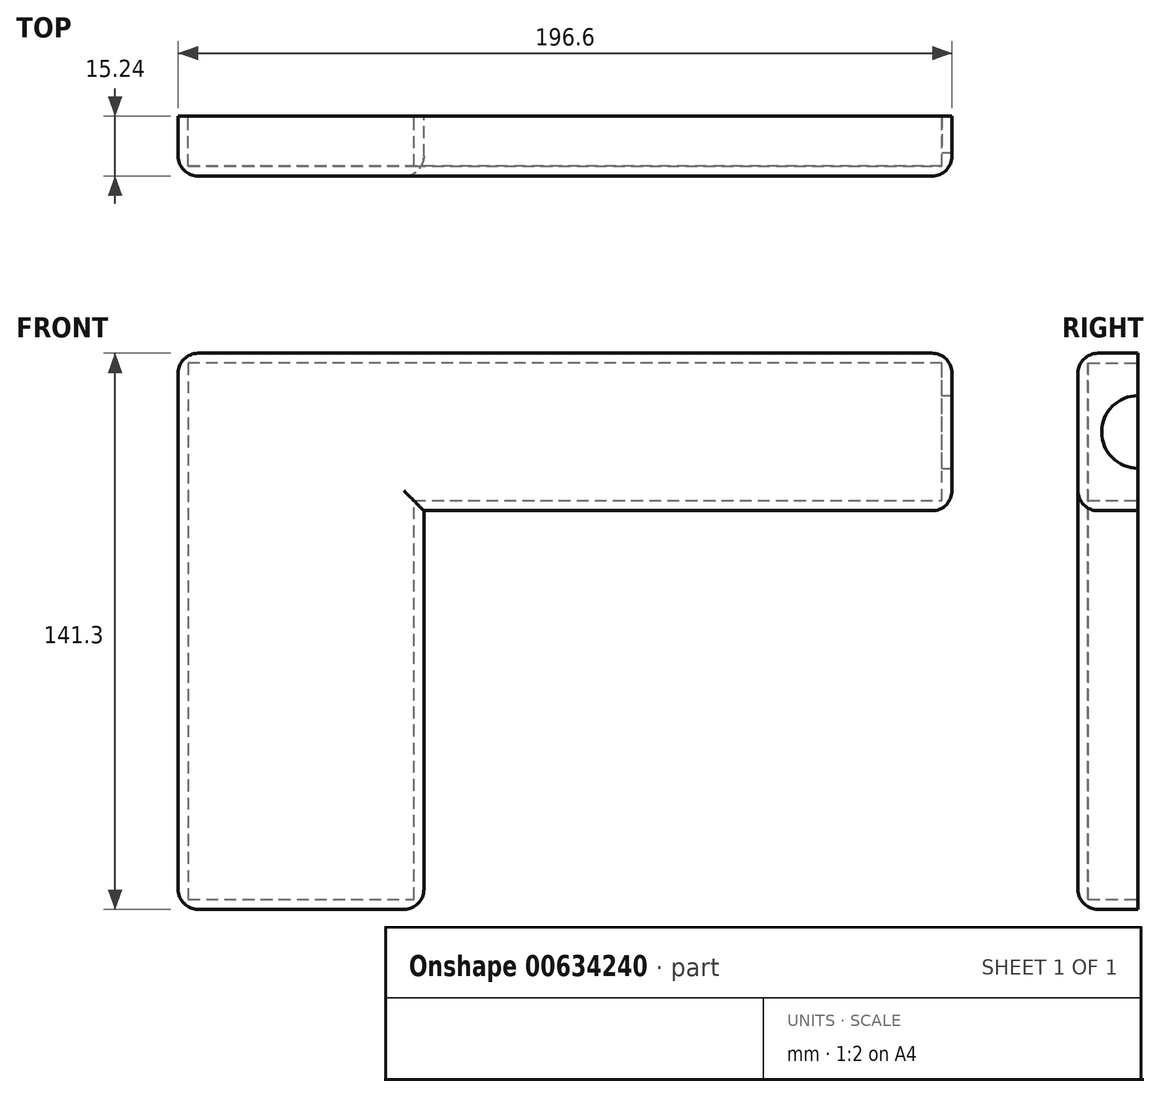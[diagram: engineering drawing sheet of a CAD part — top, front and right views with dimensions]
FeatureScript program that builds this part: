
annotation { "Feature Type Name" : "Feature", "Feature Type Description" : "" }
export const myFeature = defineFeature(function(context is Context, id is Id, definition is map)
    precondition{}
    {
        {
            var Q0;
            Q0=qCreatedBy(makeId("Front.planeOp"),FACE);
            var sketch = newSketch(context, id + "F0", { "sketchPlane" : qUnion([Q0])});
            skLineSegment(sketch, "E0", {"start": v(86.57, 57.04) * mm, "end": v(-110.03, 57.04) * mm});
            skLineSegment(sketch, "E1", {"start": v(-110.03, 57.04) * mm, "end": v(-110.03, -84.26) * mm});
            skLineSegment(sketch, "E2", {"start": v(-110.03, -84.26) * mm, "end": v(-47.62, -84.26) * mm});
            skLineSegment(sketch, "E3", {"start": v(-47.62, -84.26) * mm, "end": v(-47.62, 17.04) * mm});
            skLineSegment(sketch, "E4", {"start": v(-47.62, 17.04) * mm, "end": v(86.57, 17.04) * mm});
            skLineSegment(sketch, "E5", {"start": v(86.57, 17.04) * mm, "end": v(86.57, 57.04) * mm});
            skSolve(sketch);
        }
        {
            var Q0;
            Q0=makeQuery(id+"F0.imprint","IMPRINT",FACE,{"disambiguationData":[TD([[makeQuery(id+"F0.imprint","IMPRINT",EDGE,{"derivedFrom":sQuery(id+"F0.wireOp",EDGE,"E0")}),1.0]])]});
            extrude(context, id + "F1", {"entities" : qUnion([Q0]), "depth" : 15.24 * mm, "offsetDistance" : 25.4 * mm});
        }
        {
            var Q0;
            Q0=makeQuery(id+"F1.opExtrude","CAP_FACE",FACE,{"disambiguationData":[OSD([sQuery(id+"F0.wireOp",EDGE,"E0"),sQuery(id+"F0.wireOp",EDGE,"E1"),sQuery(id+"F0.wireOp",EDGE,"E2"),sQuery(id+"F0.wireOp",EDGE,"E3"),sQuery(id+"F0.wireOp",EDGE,"E4"),sQuery(id+"F0.wireOp",EDGE,"E5")])],"isStart":true});
            shell(context, id + "F2", {"entities" : qUnion([Q0]), "thickness" : 2.54 * mm});
        }
        {
            var Q0;
            Q0=makeQuery(id+"F1.opExtrude","CAP_EDGE",EDGE,{"disambiguationData":[OSD([sQuery(id+"F0.wireOp",EDGE,"E1")])],"isStart":false});
            var Q1;
            Q1=makeQuery(id+"F1.opExtrude","CAP_EDGE",EDGE,{"disambiguationData":[OSD([sQuery(id+"F0.wireOp",EDGE,"E3")])],"isStart":false});
            var Q2;
            Q2=makeQuery(id+"F1.opExtrude","CAP_EDGE",EDGE,{"disambiguationData":[OSD([sQuery(id+"F0.wireOp",EDGE,"E2")])],"isStart":false});
            var Q3;
            Q3=makeQuery(id+"F1.opExtrude","SWEPT_EDGE",EDGE,{"disambiguationData":[OSD([sQuery(id+"F0.wireOp",EDGE,"E1"),sQuery(id+"F0.wireOp",EDGE,"E2")])]});
            var Q4;
            Q4=makeQuery(id+"F1.opExtrude","CAP_EDGE",EDGE,{"disambiguationData":[OSD([sQuery(id+"F0.wireOp",EDGE,"E0")])],"isStart":false});
            var Q5;
            Q5=makeQuery(id+"F1.opExtrude","CAP_EDGE",EDGE,{"disambiguationData":[OSD([sQuery(id+"F0.wireOp",EDGE,"E4")])],"isStart":false});
            var Q6;
            Q6=makeQuery(id+"F1.opExtrude","SWEPT_EDGE",EDGE,{"disambiguationData":[OSD([sQuery(id+"F0.wireOp",EDGE,"E0"),sQuery(id+"F0.wireOp",EDGE,"E1")])]});
            var Q7;
            Q7=makeQuery(id+"F1.opExtrude","CAP_EDGE",EDGE,{"disambiguationData":[OSD([sQuery(id+"F0.wireOp",EDGE,"E5")])],"isStart":false});
            var Q8;
            Q8=makeQuery(id+"F1.opExtrude","SWEPT_EDGE",EDGE,{"disambiguationData":[OSD([sQuery(id+"F0.wireOp",EDGE,"E0"),sQuery(id+"F0.wireOp",EDGE,"E5")])]});
            var Q9;
            Q9=makeQuery(id+"F1.opExtrude","SWEPT_EDGE",EDGE,{"disambiguationData":[OSD([sQuery(id+"F0.wireOp",EDGE,"E4"),sQuery(id+"F0.wireOp",EDGE,"E5")])]});
            var Q10;
            Q10=makeQuery(id+"F1.opExtrude","SWEPT_EDGE",EDGE,{"disambiguationData":[OSD([sQuery(id+"F0.wireOp",EDGE,"E2"),sQuery(id+"F0.wireOp",EDGE,"E3")])]});
            var Q11;
            Q11=makeQuery(id+"F1.opExtrude","SWEPT_EDGE",EDGE,{"disambiguationData":[OSD([sQuery(id+"F0.wireOp",EDGE,"E2"),sQuery(id+"F0.wireOp",EDGE,"E3")])]});
            fillet(context, id + "F3", {"entities" : qUnion([Q0, Q1, Q2, Q3, Q4, Q5, Q6, Q7, Q8, Q9, Q10, Q11]), "radius" : 5.08 * mm, "tangentPropagation" : true, "allowEdgeOverflow" : false});
        }
        {
            var Q0;
            Q0=makeQuery(id+"F1.opExtrude","SWEPT_FACE",FACE,{"disambiguationData":[OSD([sQuery(id+"F0.wireOp",EDGE,"E5")])]});
            var sketch = newSketch(context, id + "F4", { "sketchPlane" : qUnion([Q0])});
            skCircle(sketch, "E6", {"center": v(0, 37.04) * mm, "radius": 9.23 * mm});
            skSolve(sketch);
        }
        {
            var Q0;
            Q0=sQuery(id+"F4.wireOp",VERTEX,"E6.center");
            var Q1;
            Q1=makeQuery(id+"F1.opExtrude","SWEPT_BODY",BODY,{"disambiguationData":[OSD([sQuery(id+"F0.wireOp",EDGE,"E0"),sQuery(id+"F0.wireOp",EDGE,"E1"),sQuery(id+"F0.wireOp",EDGE,"E2"),sQuery(id+"F0.wireOp",EDGE,"E3"),sQuery(id+"F0.wireOp",EDGE,"E4"),sQuery(id+"F0.wireOp",EDGE,"E5")])]});
            hole(context, id + "F5", {"style" : HoleStyle.SIMPLE, "endStyle" : HoleEndStyle.BLIND, "holeDiameter" : 18.47 * mm, "majorDiameter" : 6.35 * mm, "holeDepth" : 14 * mm, "isTappedThrough" : true, "tappedDepth" : 12.7 * mm, "tapClearance" : 3, "startFromSketch" : true, "locations" : qUnion([Q0]), "scope" : qUnion([Q1])});
        }
    });
